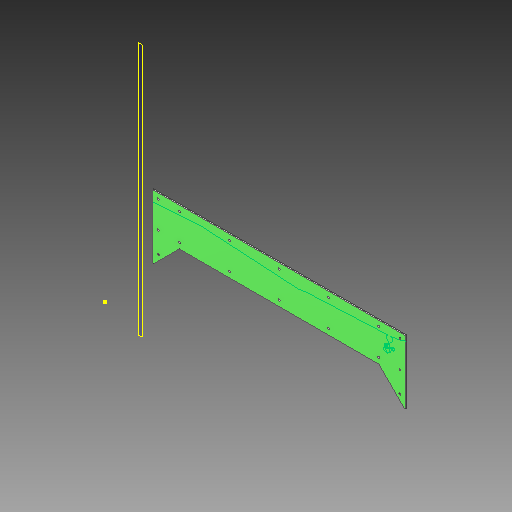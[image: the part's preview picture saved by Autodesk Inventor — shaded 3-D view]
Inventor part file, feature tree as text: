
AUTODESK INVENTOR PART (.ipt)
format: ipt  version: 2018 (Build 220112000, 112)  size: 1,236,480 bytes
history: native  units: mm
features: sketch x3, other x3, plane x1, extrude x1, hole x1, projected_geometry x1
ambient origin geometry x8: Origin, YZ Plane, XZ Plane, XY Plane, X Axis, Y Axis, Z Axis, Center Point
bodies: Solid1 (feature_tree)
feature tree (10):
  plane  "Work Plane1"
  extrude  "Extrusion1"  [1 undecoded]
  sketch  "Sketch2"  dims[d2=5.2mm d3=6.0mm d4=4.0mm d5=2.0mm d6=90.0deg d7=8.0mm d8=20.594885mm]
  hole  "Hole1"  [1 undecoded]
  sketch  "Sketch1"  dims[d0=3.0mm d1=0.0mm]
  sketch  "Sketch3"
  projected_geometry  "Projected Loop1"
  other  "<userpath>\OneDrive\Inventor\Beast 3D Printer\Main assembly Test.iam"
  other  "Main assembly Test.iam"
  other  "3030 600mm:6"
note: 2 required parameter values undecoded (feature->parameter linkage not recoverable at this tier; creation-order binding heuristic only, values carry confidence <= 0.55)
